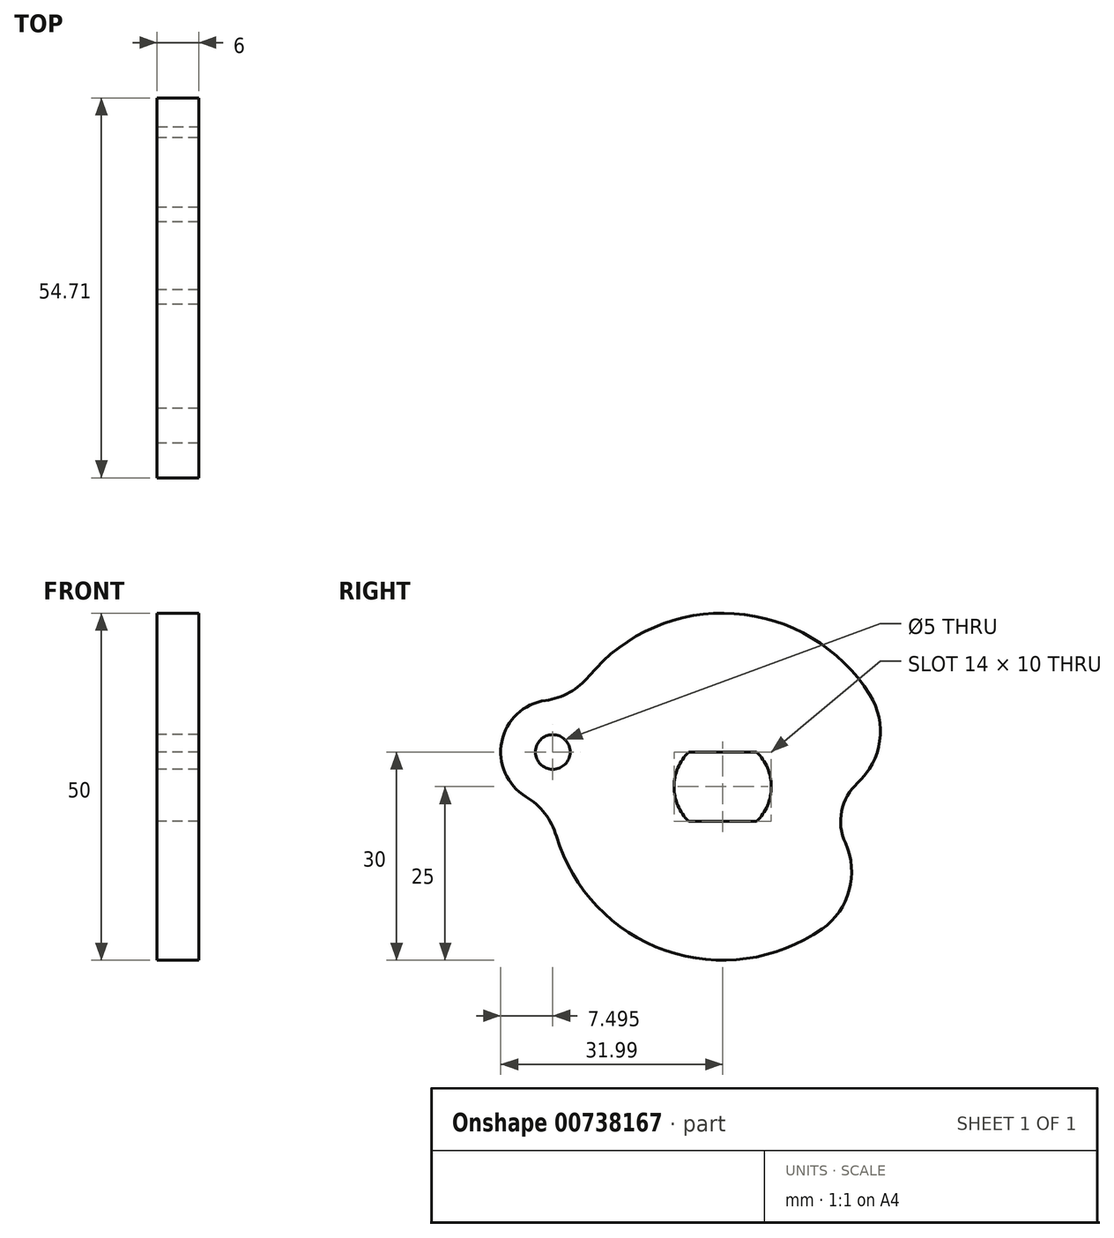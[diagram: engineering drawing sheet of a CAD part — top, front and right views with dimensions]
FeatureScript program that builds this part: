
annotation { "Feature Type Name" : "Feature", "Feature Type Description" : "" }
export const myFeature = defineFeature(function(context is Context, id is Id, definition is map)
    precondition{}
    {
        {
            var Q0;
            Q0=qCreatedBy(makeId("Right.planeOp"),FACE);
            var sketch = newSketch(context, id + "F0", { "sketchPlane" : qUnion([Q0])});
            skCircle(sketch, "E0", {"center": v(0, 0) * mm, "radius": 7 * mm});
            skPoint(sketch, "E1", {"position": v(-4.9, 5) * mm});
            skPoint(sketch, "E2", {"position": v(4.9, 5) * mm});
            skPoint(sketch, "E3", {"position": v(4.9, -5) * mm});
            skPoint(sketch, "E4", {"position": v(-4.9, -5) * mm});
            skLineSegment(sketch, "E5", {"start": v(-4.9, 5) * mm, "end": v(4.9, 5) * mm});
            skLineSegment(sketch, "E6", {"start": v(-4.9, -5) * mm, "end": v(4.9, -5) * mm});
            skCircle(sketch, "E7", {"center": v(0, 0) * mm, "radius": 25 * mm});
            skCircle(sketch, "E8", {"center": v(24.5, -5) * mm, "radius": 2 * mm});
            skCircle(sketch, "E9", {"center": v(24.5, -5) * mm, "radius": 7.5 * mm});
            skCircle(sketch, "E10", {"center": v(-24.5, 5) * mm, "radius": 2.5 * mm});
            skCircle(sketch, "E11", {"center": v(-24.5, 5) * mm, "radius": 7.5 * mm});
            skSolve(sketch);
        }
        {
            var Q0;
            {var subQ0=sQuery(id+"F0.wireOp",EDGE,"E5");var subQ1=sQuery(id+"F0.wireOp",EDGE,"E0");var subQ6=makeQuery(id+"F0.imprint","INTERSECT",VERTEX,{"disambiguationData":[OD(0.0)],"derivedFrom":[subQ1,subQ0]});Q0=makeQuery(id+"F0.imprint","IMPRINT",FACE,{"disambiguationData":[TD([[makeQuery(id+"F0.imprint","IMPRINT",EDGE,{"disambiguationData":[TD([[subQ6,1.0]])],"derivedFrom":subQ1}),-1.0]])]});}
            var Q1;
            {var subQ0=sQuery(id+"F0.wireOp",EDGE,"E11");var subQ1=sQuery(id+"F0.wireOp",EDGE,"E7");var subQ2=makeQuery(id+"F0.imprint","INTERSECT",VERTEX,{"disambiguationData":[OD(0.0)],"derivedFrom":[subQ1,subQ0]});Q1=makeQuery(id+"F0.imprint","IMPRINT",FACE,{"disambiguationData":[TD([[makeQuery(id+"F0.imprint","IMPRINT",EDGE,{"disambiguationData":[TD([[subQ2,-1.0]])],"derivedFrom":subQ1}),1.0]])]});}
            var Q2;
            {var subQ0=sQuery(id+"F0.wireOp",EDGE,"E11");var subQ1=sQuery(id+"F0.wireOp",EDGE,"E7");var subQ2=makeQuery(id+"F0.imprint","INTERSECT",VERTEX,{"disambiguationData":[OD(0.0)],"derivedFrom":[subQ1,subQ0]});Q2=makeQuery(id+"F0.imprint","IMPRINT",FACE,{"disambiguationData":[TD([[makeQuery(id+"F0.imprint","IMPRINT",EDGE,{"disambiguationData":[TD([[subQ2,-1.0]])],"derivedFrom":subQ1}),-1.0]])]});}
            var Q3;
            {var subQ0=sQuery(id+"F0.wireOp",EDGE,"E6");Q3=makeQuery(id+"F0.imprint","IMPRINT",FACE,{"disambiguationData":[TD([[makeQuery(id+"F0.imprint","IMPRINT",EDGE,{"derivedFrom":subQ0}),-1.0]])]});}
            var Q4;
            {var subQ0=sQuery(id+"F0.wireOp",EDGE,"E5");Q4=makeQuery(id+"F0.imprint","IMPRINT",FACE,{"disambiguationData":[TD([[makeQuery(id+"F0.imprint","IMPRINT",EDGE,{"derivedFrom":subQ0}),1.0]])]});}
            var Q5;
            {var subQ0=sQuery(id+"F0.wireOp",EDGE,"E9");var subQ1=sQuery(id+"F0.wireOp",EDGE,"E7");var subQ2=makeQuery(id+"F0.imprint","INTERSECT",VERTEX,{"disambiguationData":[OD(1.0)],"derivedFrom":[subQ1,subQ0]});Q5=makeQuery(id+"F0.imprint","IMPRINT",FACE,{"disambiguationData":[TD([[makeQuery(id+"F0.imprint","IMPRINT",EDGE,{"disambiguationData":[TD([[subQ2,-1.0]])],"derivedFrom":subQ1}),-1.0]])]});}
            var Q6;
            {var subQ0=sQuery(id+"F0.wireOp",EDGE,"E9");var subQ1=sQuery(id+"F0.wireOp",EDGE,"E7");var subQ2=makeQuery(id+"F0.imprint","INTERSECT",VERTEX,{"disambiguationData":[OD(1.0)],"derivedFrom":[subQ1,subQ0]});Q6=makeQuery(id+"F0.imprint","IMPRINT",FACE,{"disambiguationData":[TD([[makeQuery(id+"F0.imprint","IMPRINT",EDGE,{"disambiguationData":[TD([[subQ2,-1.0]])],"derivedFrom":subQ1}),1.0]])]});}
            extrude(context, id + "F1", {"entities" : qUnion([Q0, Q1, Q2, Q3, Q4, Q5, Q6]), "depth" : 6 * mm, "offsetDistance" : 25 * mm});
        }
        {
            var Q0;
            {var subQ0=sQuery(id+"F0.wireOp",EDGE,"E9");var subQ1=sQuery(id+"F0.wireOp",EDGE,"E7");Q0=makeQuery(id+"F1.opExtrude","SWEPT_EDGE",EDGE,{"disambiguationData":[OSD([subQ1,subQ0]),TDD([makeQuery(id+"F0.imprint","INTERSECT",VERTEX,{"disambiguationData":[OD(0.0)],"derivedFrom":[subQ1,subQ0]})])]});}
            var Q1;
            {var subQ0=sQuery(id+"F0.wireOp",EDGE,"E9");var subQ1=sQuery(id+"F0.wireOp",EDGE,"E7");Q1=makeQuery(id+"F1.opExtrude","SWEPT_EDGE",EDGE,{"disambiguationData":[OSD([subQ1,subQ0]),TDD([makeQuery(id+"F0.imprint","INTERSECT",VERTEX,{"disambiguationData":[OD(1.0)],"derivedFrom":[subQ1,subQ0]})])]});}
            var Q2;
            {var subQ0=sQuery(id+"F0.wireOp",EDGE,"E11");var subQ1=sQuery(id+"F0.wireOp",EDGE,"E7");Q2=makeQuery(id+"F1.opExtrude","SWEPT_EDGE",EDGE,{"disambiguationData":[OSD([subQ1,subQ0]),TDD([makeQuery(id+"F0.imprint","INTERSECT",VERTEX,{"disambiguationData":[OD(0.0)],"derivedFrom":[subQ1,subQ0]})])]});}
            var Q3;
            {var subQ0=sQuery(id+"F0.wireOp",EDGE,"E11");var subQ1=sQuery(id+"F0.wireOp",EDGE,"E7");Q3=makeQuery(id+"F1.opExtrude","SWEPT_EDGE",EDGE,{"disambiguationData":[OSD([subQ1,subQ0]),TDD([makeQuery(id+"F0.imprint","INTERSECT",VERTEX,{"disambiguationData":[OD(1.0)],"derivedFrom":[subQ1,subQ0]})])]});}
            fillet(context, id + "F2", {"entities" : qUnion([Q0, Q1, Q2, Q3]), "radius" : 10 * mm, "tangentPropagation" : true, "allowEdgeOverflow" : false});
        }
    });
